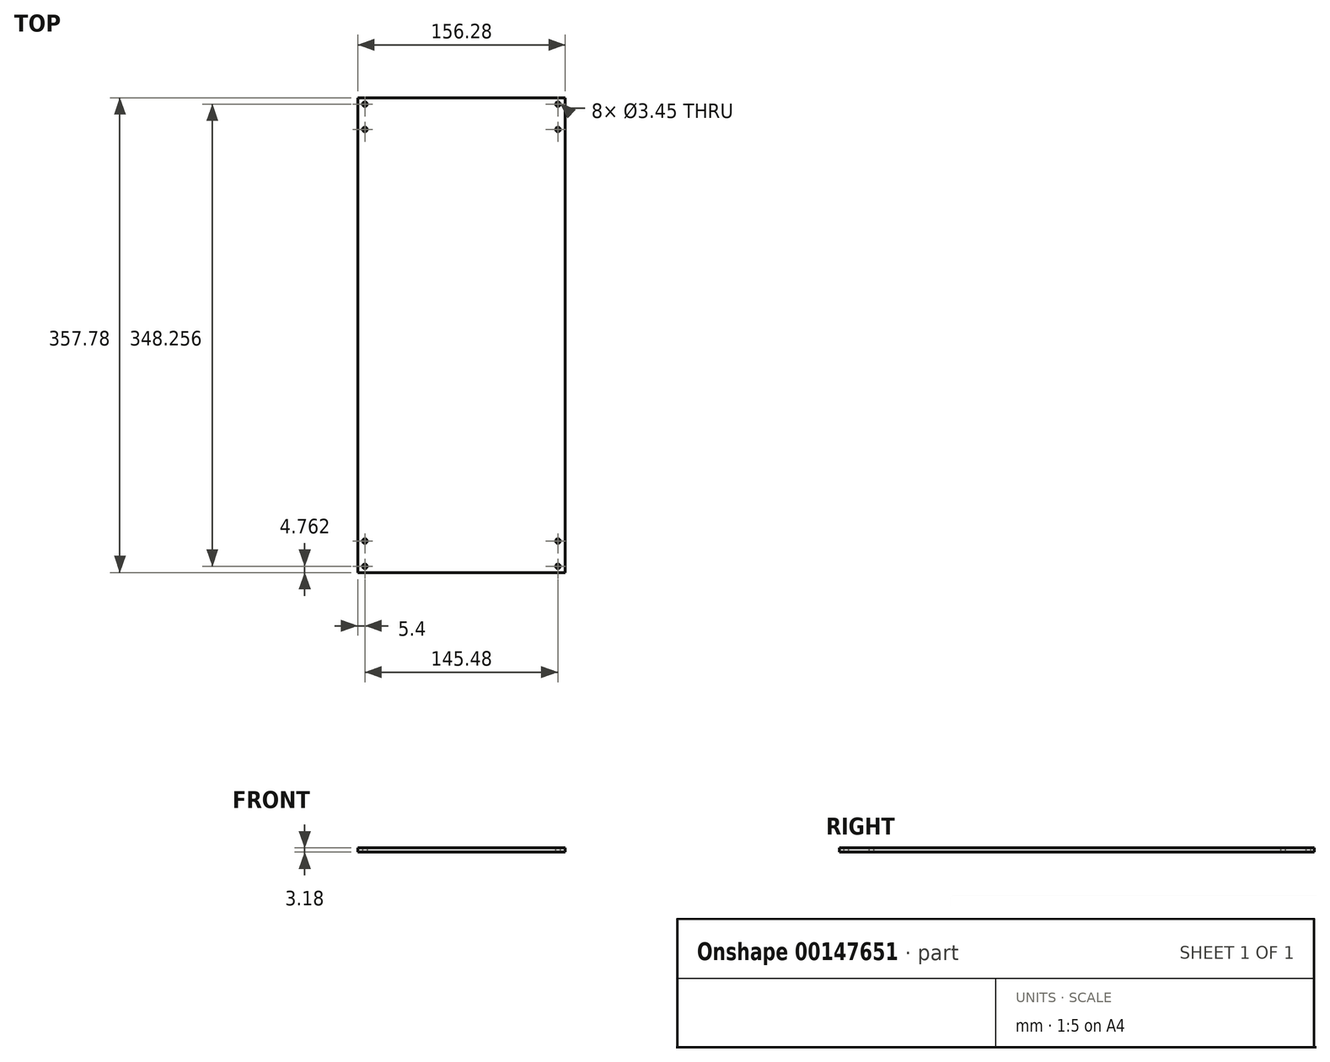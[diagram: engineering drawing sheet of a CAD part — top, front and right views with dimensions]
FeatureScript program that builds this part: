
annotation { "Feature Type Name" : "Feature", "Feature Type Description" : "" }
export const myFeature = defineFeature(function(context is Context, id is Id, definition is map)
    precondition{}
    {
        {
            var Q0;
            Q0=qCreatedBy(makeId("Top.planeOp"),FACE);
            var sketch = newSketch(context, id + "F0", { "sketchPlane" : qUnion([Q0])});
            skLineSegment(sketch, "E0.bottom", {"start": v(78.14, -178.9) * mm, "end": v(-78.14, -178.9) * mm});
            skLineSegment(sketch, "E0.top", {"start": v(78.14, 178.9) * mm, "end": v(-78.14, 178.9) * mm});
            skLineSegment(sketch, "E0.left", {"start": v(78.14, -178.9) * mm, "end": v(78.14, 178.9) * mm});
            skLineSegment(sketch, "E0.right", {"start": v(-78.14, -178.9) * mm, "end": v(-78.14, 178.9) * mm});
            skPoint(sketch, "E0.middle", {"position": v(0, 0) * mm});
            skLineSegment(sketch, "E1", {"start": v(72.74, 155.08) * mm, "end": v(78.14, 155.08) * mm, "construction": true});
            skLineSegment(sketch, "E2.bottom", {"start": v(72.74, 155.08) * mm, "end": v(-72.74, 155.08) * mm, "construction": true});
            skLineSegment(sketch, "E2.top", {"start": v(72.74, -155.08) * mm, "end": v(-72.74, -155.08) * mm, "construction": true});
            skLineSegment(sketch, "E2.left", {"start": v(72.74, 155.08) * mm, "end": v(72.74, -155.08) * mm, "construction": true});
            skLineSegment(sketch, "E2.right", {"start": v(-72.74, 155.08) * mm, "end": v(-72.74, -155.08) * mm, "construction": true});
            skCircle(sketch, "E3", {"center": v(72.74, 155.08) * mm, "radius": 1.73 * mm});
            skCircle(sketch, "E4", {"center": v(-72.74, -155.08) * mm, "radius": 1.73 * mm});
            skLineSegment(sketch, "E5", {"start": v(0, 155.08) * mm, "end": v(0, 178.9) * mm, "construction": true});
            skLineSegment(sketch, "E6", {"start": v(72.74, 155.08) * mm, "end": v(72.74, 174.13) * mm, "construction": true});
            skCircle(sketch, "E7", {"center": v(-72.74, 155.08) * mm, "radius": 1.73 * mm});
            skCircle(sketch, "E8", {"center": v(72.74, -155.08) * mm, "radius": 1.73 * mm});
            skLineSegment(sketch, "E9", {"start": v(72.74, 174.13) * mm, "end": v(72.74, 178.9) * mm, "construction": true});
            skCircle(sketch, "E10", {"center": v(72.74, 174.13) * mm, "radius": 1.73 * mm});
            skLineSegment(sketch, "E11", {"start": v(-72.74, 155.08) * mm, "end": v(-72.74, 174.13) * mm, "construction": true});
            skLineSegment(sketch, "E12", {"start": v(-72.74, 174.13) * mm, "end": v(-72.74, 178.9) * mm, "construction": true});
            skLineSegment(sketch, "E13", {"start": v(-72.74, -155.08) * mm, "end": v(-72.74, -174.13) * mm, "construction": true});
            skLineSegment(sketch, "E14", {"start": v(-72.74, -174.13) * mm, "end": v(-72.74, -178.9) * mm, "construction": true});
            skLineSegment(sketch, "E15", {"start": v(72.74, -155.08) * mm, "end": v(72.74, -174.13) * mm, "construction": true});
            skLineSegment(sketch, "E16", {"start": v(72.74, -174.13) * mm, "end": v(72.74, -178.9) * mm, "construction": true});
            skCircle(sketch, "E17", {"center": v(-72.74, 174.13) * mm, "radius": 1.73 * mm});
            skCircle(sketch, "E18", {"center": v(-72.74, -174.13) * mm, "radius": 1.73 * mm});
            skCircle(sketch, "E19", {"center": v(72.74, -174.13) * mm, "radius": 1.73 * mm});
            skSolve(sketch);
        }
        {
            var Q0;
            Q0=makeQuery(id+"F0.imprint","IMPRINT",FACE,{"disambiguationData":[TD([[makeQuery(id+"F0.imprint","IMPRINT",EDGE,{"derivedFrom":sQuery(id+"F0.wireOp",EDGE,"E0.bottom")}),-1.0]])]});
            extrude(context, id + "F1", {"entities" : qUnion([Q0]), "depth" : 3.17 * mm});
        }
    });
